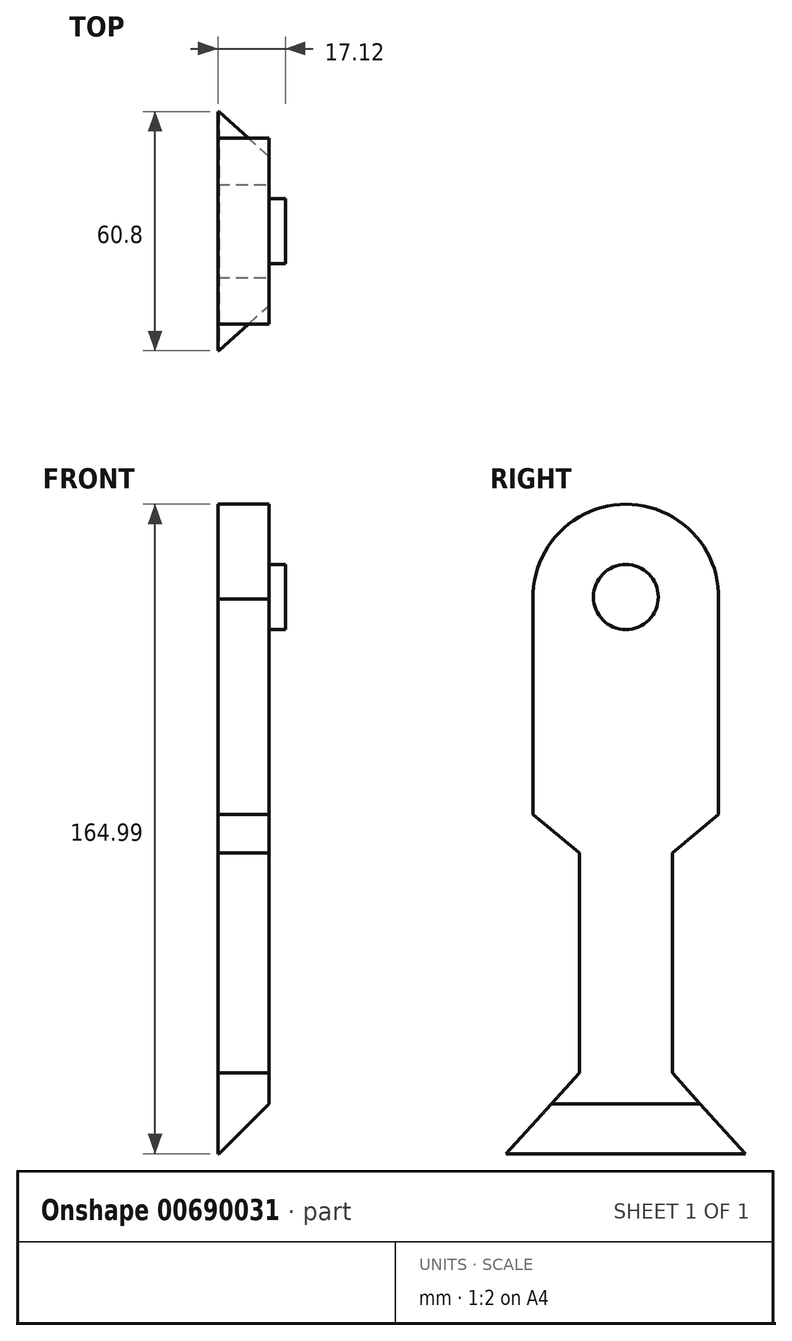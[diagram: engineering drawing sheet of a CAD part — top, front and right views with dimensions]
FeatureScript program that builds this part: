
annotation { "Feature Type Name" : "Feature", "Feature Type Description" : "" }
export const myFeature = defineFeature(function(context is Context, id is Id, definition is map)
    precondition{}
    {
        {
            var Q0;
            Q0=qCreatedBy(makeId("Right.planeOp"),FACE);
            var sketch = newSketch(context, id + "F0", { "sketchPlane" : qUnion([Q0])});
            skCircle(sketch, "E0.0", {"center": v(0, -36.2) * mm, "radius": 8.26 * mm});
            skSolve(sketch);
        }
        {
            var Q0;
            Q0=makeQuery(id+"F0.imprint","IMPRINT",FACE,{"disambiguationData":[TD([[makeQuery(id+"F0.imprint","IMPRINT",EDGE,{"derivedFrom":sQuery(id+"F0.wireOp",EDGE,"E0.0")}),1.0]])]});
            extrude(context, id + "F1", {"entities" : qUnion([Q0]), "oppositeDirection" : true, "depth" : 4.2 * mm, "offsetDistance" : 25.4 * mm});
        }
        {
            var Q0;
            Q0=makeQuery(id+"F1.opExtrude","CAP_FACE",FACE,{"disambiguationData":[OSD([sQuery(id+"F0.wireOp",EDGE,"E0.0")])],"isStart":false});
            var sketch = newSketch(context, id + "F2", { "sketchPlane" : qUnion([Q0])});
            skArc(sketch, "E1.0", {"start": v(-23.57, -36.74) * mm, "mid": v(0, -12.62) * mm, "end": v(23.57, -36.74) * mm});
            skLineSegment(sketch, "E2.0", {"start": v(-23.57, -36.74) * mm, "end": v(-23.57, -91.46) * mm});
            skLineSegment(sketch, "E3.0", {"start": v(-23.57, -91.46) * mm, "end": v(-11.78, -101.2) * mm});
            skLineSegment(sketch, "E4.0", {"start": v(23.57, -36.74) * mm, "end": v(23.57, -91.46) * mm});
            skLineSegment(sketch, "E5.0", {"start": v(23.57, -91.46) * mm, "end": v(11.78, -101.2) * mm});
            skLineSegment(sketch, "E6.0", {"start": v(11.78, -101.2) * mm, "end": v(11.78, -157.08) * mm});
            skLineSegment(sketch, "E7.0", {"start": v(-11.78, -101.2) * mm, "end": v(-11.78, -157.08) * mm});
            skLineSegment(sketch, "E8.0", {"start": v(-30.4, -177.6) * mm, "end": v(-18.88, -164.9) * mm});
            skLineSegment(sketch, "E9.0", {"start": v(-11.78, -157.08) * mm, "end": v(-18.88, -164.9) * mm});
            skLineSegment(sketch, "E10.0", {"start": v(30.4, -177.6) * mm, "end": v(-30.4, -177.6) * mm});
            skLineSegment(sketch, "E11.0", {"start": v(18.88, -164.9) * mm, "end": v(30.4, -177.6) * mm});
            skLineSegment(sketch, "E12.0", {"start": v(11.78, -157.08) * mm, "end": v(18.88, -164.9) * mm});
            skSolve(sketch);
        }
        {
            var Q0;
            Q0 = qSketchRegion(id + "F2", true);
            extrude(context, id + "F3", {"entities" : qUnion([Q0]), "operationType" : NewBodyOperationType.ADD, "depth" : 12.93 * mm, "offsetDistance" : 25.4 * mm});
        }
        {
            var Q0;
            Q0=makeQuery(id+"F3.opExtrude","CAP_EDGE",EDGE,{"disambiguationData":[OSD([sQuery(id+"F2.wireOp",EDGE,"E10.0")])],"isStart":true});
            chamfer(context, id + "F4", {"entities" : qUnion([Q0]), "width" : 12.7 * mm, "tangentPropagation" : true});
        }
    });
